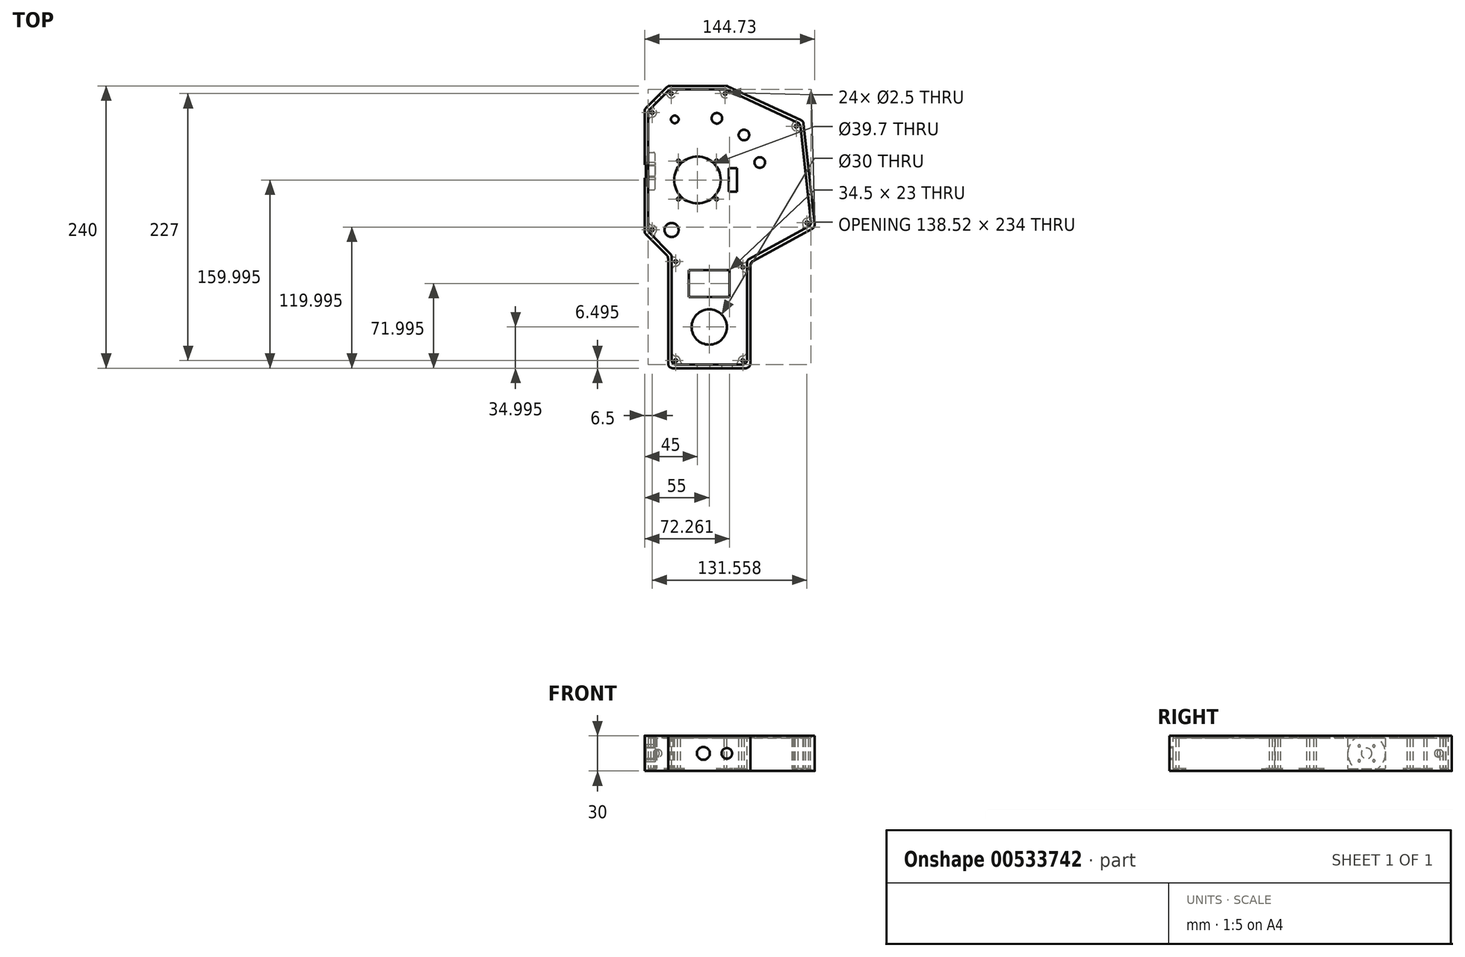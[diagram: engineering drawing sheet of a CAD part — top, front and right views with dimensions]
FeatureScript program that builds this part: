
annotation { "Feature Type Name" : "Feature", "Feature Type Description" : "" }
export const myFeature = defineFeature(function(context is Context, id is Id, definition is map)
    precondition{}
    {
        {
            var Q0;
            Q0=qCreatedBy(makeId("Top.planeOp"),FACE);
            var sketch = newSketch(context, id + "F0", { "sketchPlane" : qUnion([Q0])});
            skLineSegment(sketch, "E0", {"start": v(-66.45, 92.82) * mm, "end": v(-16.45, 92.82) * mm});
            skLineSegment(sketch, "E1", {"start": v(-16.45, 92.82) * mm, "end": v(48.55, 62.82) * mm});
            skLineSegment(sketch, "E2", {"start": v(48.55, 62.82) * mm, "end": v(58.55, -27.18) * mm});
            skLineSegment(sketch, "E3", {"start": v(58.55, -27.18) * mm, "end": v(3.55, -57.18) * mm});
            skLineSegment(sketch, "E4", {"start": v(3.55, -57.18) * mm, "end": v(3.55, -147.18) * mm});
            skLineSegment(sketch, "E5", {"start": v(3.55, -147.18) * mm, "end": v(-66.45, -147.18) * mm});
            skLineSegment(sketch, "E6", {"start": v(-66.45, -147.18) * mm, "end": v(-66.45, -52.18) * mm});
            skLineSegment(sketch, "E7", {"start": v(-66.45, -52.18) * mm, "end": v(-86.45, -32.18) * mm});
            skLineSegment(sketch, "E8", {"start": v(-86.45, -32.18) * mm, "end": v(-86.45, 72.82) * mm});
            skLineSegment(sketch, "E9", {"start": v(-86.45, 72.82) * mm, "end": v(-66.45, 92.82) * mm});
            skLineSegment(sketch, "E10.0", {"start": v(55.35, -25.52) * mm, "end": v(0.55, -55.4) * mm});
            skLineSegment(sketch, "E10.1", {"start": v(45.76, 60.8) * mm, "end": v(55.35, -25.52) * mm});
            skLineSegment(sketch, "E10.2", {"start": v(0.55, -55.4) * mm, "end": v(0.55, -144.18) * mm});
            skLineSegment(sketch, "E10.3", {"start": v(-17.1, 89.82) * mm, "end": v(45.76, 60.8) * mm});
            skLineSegment(sketch, "E10.4", {"start": v(-65.2, 89.82) * mm, "end": v(-17.1, 89.82) * mm});
            skLineSegment(sketch, "E10.5", {"start": v(-83.45, 71.57) * mm, "end": v(-65.2, 89.82) * mm});
            skLineSegment(sketch, "E10.6", {"start": v(0.55, -144.18) * mm, "end": v(-63.45, -144.18) * mm});
            skLineSegment(sketch, "E10.7", {"start": v(-63.45, -144.18) * mm, "end": v(-63.45, -50.94) * mm});
            skLineSegment(sketch, "E10.8", {"start": v(-63.45, -50.94) * mm, "end": v(-83.45, -30.94) * mm});
            skLineSegment(sketch, "E10.9", {"start": v(-83.45, -30.94) * mm, "end": v(-83.45, 71.57) * mm});
            skSolve(sketch);
        }
        {
            var Q0;
            Q0=makeQuery(id+"F0.imprint","IMPRINT",FACE,{"disambiguationData":[TD([[makeQuery(id+"F0.imprint","IMPRINT",EDGE,{"derivedFrom":sQuery(id+"F0.wireOp",EDGE,"E0")}),-1.0]])]});
            extrude(context, id + "F1", {"entities" : qUnion([Q0]), "endBound" : BoundingType.SYMMETRIC, "depth" : 30 * mm, "offsetDistance" : 25 * mm});
        }
        {
            var Q0;
            Q0=makeQuery(id+"F1.opExtrude","SWEPT_EDGE",EDGE,{"disambiguationData":[OSD([sQuery(id+"F0.wireOp",EDGE,"E4"),sQuery(id+"F0.wireOp",EDGE,"E5")])]});
            var Q1;
            Q1=makeQuery(id+"F1.opExtrude","SWEPT_EDGE",EDGE,{"disambiguationData":[OSD([sQuery(id+"F0.wireOp",EDGE,"E5"),sQuery(id+"F0.wireOp",EDGE,"E6")])]});
            var Q2;
            Q2=makeQuery(id+"F1.opExtrude","SWEPT_EDGE",EDGE,{"disambiguationData":[OSD([sQuery(id+"F0.wireOp",EDGE,"E6"),sQuery(id+"F0.wireOp",EDGE,"E7")])]});
            var Q3;
            Q3=makeQuery(id+"F1.opExtrude","SWEPT_EDGE",EDGE,{"disambiguationData":[OSD([sQuery(id+"F0.wireOp",EDGE,"E7"),sQuery(id+"F0.wireOp",EDGE,"E8")])]});
            var Q4;
            Q4=makeQuery(id+"F1.opExtrude","SWEPT_EDGE",EDGE,{"disambiguationData":[OSD([sQuery(id+"F0.wireOp",EDGE,"E8"),sQuery(id+"F0.wireOp",EDGE,"E9")])]});
            var Q5;
            Q5=makeQuery(id+"F1.opExtrude","SWEPT_EDGE",EDGE,{"disambiguationData":[OSD([sQuery(id+"F0.wireOp",EDGE,"E0"),sQuery(id+"F0.wireOp",EDGE,"E9")])]});
            var Q6;
            Q6=makeQuery(id+"F1.opExtrude","SWEPT_EDGE",EDGE,{"disambiguationData":[OSD([sQuery(id+"F0.wireOp",EDGE,"E0"),sQuery(id+"F0.wireOp",EDGE,"E1")])]});
            var Q7;
            Q7=makeQuery(id+"F1.opExtrude","SWEPT_EDGE",EDGE,{"disambiguationData":[OSD([sQuery(id+"F0.wireOp",EDGE,"E1"),sQuery(id+"F0.wireOp",EDGE,"E2")])]});
            var Q8;
            Q8=makeQuery(id+"F1.opExtrude","SWEPT_EDGE",EDGE,{"disambiguationData":[OSD([sQuery(id+"F0.wireOp",EDGE,"E2"),sQuery(id+"F0.wireOp",EDGE,"E3")])]});
            var Q9;
            Q9=makeQuery(id+"F1.opExtrude","SWEPT_EDGE",EDGE,{"disambiguationData":[OSD([sQuery(id+"F0.wireOp",EDGE,"E3"),sQuery(id+"F0.wireOp",EDGE,"E4")])]});
            var Q10;
            Q10=makeQuery(id+"F1.opExtrude","SWEPT_EDGE",EDGE,{"disambiguationData":[OSD([sQuery(id+"F0.wireOp",EDGE,"E10.5"),sQuery(id+"F0.wireOp",EDGE,"E10.9")])]});
            var Q11;
            Q11=makeQuery(id+"F1.opExtrude","SWEPT_EDGE",EDGE,{"disambiguationData":[OSD([sQuery(id+"F0.wireOp",EDGE,"E10.4"),sQuery(id+"F0.wireOp",EDGE,"E10.5")])]});
            var Q12;
            Q12=makeQuery(id+"F1.opExtrude","SWEPT_EDGE",EDGE,{"disambiguationData":[OSD([sQuery(id+"F0.wireOp",EDGE,"E10.3"),sQuery(id+"F0.wireOp",EDGE,"E10.4")])]});
            var Q13;
            Q13=makeQuery(id+"F1.opExtrude","SWEPT_EDGE",EDGE,{"disambiguationData":[OSD([sQuery(id+"F0.wireOp",EDGE,"E10.1"),sQuery(id+"F0.wireOp",EDGE,"E10.3")])]});
            var Q14;
            Q14=makeQuery(id+"F1.opExtrude","SWEPT_EDGE",EDGE,{"disambiguationData":[OSD([sQuery(id+"F0.wireOp",EDGE,"E10.0"),sQuery(id+"F0.wireOp",EDGE,"E10.1")])]});
            var Q15;
            Q15=makeQuery(id+"F1.opExtrude","SWEPT_EDGE",EDGE,{"disambiguationData":[OSD([sQuery(id+"F0.wireOp",EDGE,"E10.0"),sQuery(id+"F0.wireOp",EDGE,"E10.2")])]});
            var Q16;
            Q16=makeQuery(id+"F1.opExtrude","SWEPT_EDGE",EDGE,{"disambiguationData":[OSD([sQuery(id+"F0.wireOp",EDGE,"E10.7"),sQuery(id+"F0.wireOp",EDGE,"E10.8")])]});
            var Q17;
            Q17=makeQuery(id+"F1.opExtrude","SWEPT_EDGE",EDGE,{"disambiguationData":[OSD([sQuery(id+"F0.wireOp",EDGE,"E10.8"),sQuery(id+"F0.wireOp",EDGE,"E10.9")])]});
            var Q18;
            Q18=makeQuery(id+"F1.opExtrude","SWEPT_EDGE",EDGE,{"disambiguationData":[OSD([sQuery(id+"F0.wireOp",EDGE,"E10.6"),sQuery(id+"F0.wireOp",EDGE,"E10.7")])]});
            var Q19;
            Q19=makeQuery(id+"F1.opExtrude","SWEPT_EDGE",EDGE,{"disambiguationData":[OSD([sQuery(id+"F0.wireOp",EDGE,"E10.2"),sQuery(id+"F0.wireOp",EDGE,"E10.6")])]});
            fillet(context, id + "F2", {"entities" : qUnion([Q0, Q1, Q2, Q3, Q4, Q5, Q6, Q7, Q8, Q9, Q10, Q11, Q12, Q13, Q14, Q15, Q16, Q17, Q18, Q19]), "radius" : 4 * mm, "tangentPropagation" : true, "allowEdgeOverflow" : false});
        }
        {
            var Q0;
            Q0=qCreatedBy(makeId("Top.planeOp"),FACE);
            var sketch = newSketch(context, id + "F3", { "sketchPlane" : qUnion([Q0])});
            skLineSegment(sketch, "E11.0", {"start": v(-84.95, -31.56) * mm, "end": v(-84.95, 72.2) * mm, "construction": true});
            skLineSegment(sketch, "E11.1", {"start": v(-64.95, -51.56) * mm, "end": v(-84.95, -31.56) * mm, "construction": true});
            skLineSegment(sketch, "E11.2", {"start": v(-84.95, 72.2) * mm, "end": v(-65.83, 91.32) * mm, "construction": true});
            skLineSegment(sketch, "E11.3", {"start": v(-64.95, -145.68) * mm, "end": v(-64.95, -51.56) * mm, "construction": true});
            skLineSegment(sketch, "E11.4", {"start": v(2.05, -145.68) * mm, "end": v(-64.95, -145.68) * mm, "construction": true});
            skLineSegment(sketch, "E11.5", {"start": v(2.05, -56.3) * mm, "end": v(2.05, -145.68) * mm, "construction": true});
            skLineSegment(sketch, "E11.6", {"start": v(-65.83, 91.32) * mm, "end": v(-16.78, 91.32) * mm, "construction": true});
            skLineSegment(sketch, "E11.7", {"start": v(-16.78, 91.32) * mm, "end": v(47.15, 61.8) * mm, "construction": true});
            skLineSegment(sketch, "E11.8", {"start": v(47.15, 61.8) * mm, "end": v(56.95, -26.35) * mm, "construction": true});
            skLineSegment(sketch, "E11.9", {"start": v(56.95, -26.35) * mm, "end": v(2.05, -56.3) * mm, "construction": true});
            skSolve(sketch);
        }
        {
            var Q0;
            Q0=qCreatedBy(makeId("Top.planeOp"),FACE);
            var sketch = newSketch(context, id + "F4", { "sketchPlane" : qUnion([Q0])});
            skCircle(sketch, "E12", {"center": v(-79.95, 70.12) * mm, "radius": 3.75 * mm});
            skCircle(sketch, "E13", {"center": v(-79.95, 70.12) * mm, "radius": 1.25 * mm});
            skCircle(sketch, "E14", {"center": v(-63.76, 86.32) * mm, "radius": 3.75 * mm});
            skCircle(sketch, "E15", {"center": v(-63.76, 86.32) * mm, "radius": 1.25 * mm});
            skCircle(sketch, "E16", {"center": v(-17.88, 86.32) * mm, "radius": 3.75 * mm});
            skCircle(sketch, "E17", {"center": v(-17.88, 86.32) * mm, "radius": 1.25 * mm});
            skCircle(sketch, "E18", {"center": v(42.5, 58.45) * mm, "radius": 3.75 * mm});
            skCircle(sketch, "E19", {"center": v(42.5, 58.45) * mm, "radius": 1.25 * mm});
            skCircle(sketch, "E20", {"center": v(51.6, -23.57) * mm, "radius": 3.75 * mm});
            skCircle(sketch, "E21", {"center": v(51.6, -23.57) * mm, "radius": 1.25 * mm});
            skCircle(sketch, "E22", {"center": v(-2.95, -140.68) * mm, "radius": 3.75 * mm});
            skCircle(sketch, "E23", {"center": v(-2.95, -140.68) * mm, "radius": 1.25 * mm});
            skCircle(sketch, "E24", {"center": v(-59.95, -140.68) * mm, "radius": 3.75 * mm});
            skCircle(sketch, "E25", {"center": v(-59.95, -140.68) * mm, "radius": 1.25 * mm});
            skCircle(sketch, "E26", {"center": v(-79.95, -29.5) * mm, "radius": 3.75 * mm});
            skCircle(sketch, "E27", {"center": v(-79.95, -29.5) * mm, "radius": 1.25 * mm});
            skCircle(sketch, "E28", {"center": v(-59.95, -56.56) * mm, "radius": 3.75 * mm});
            skCircle(sketch, "E29", {"center": v(-59.95, -56.56) * mm, "radius": 1.25 * mm});
            skCircle(sketch, "E30", {"center": v(-2.95, -61.3) * mm, "radius": 3.75 * mm});
            skCircle(sketch, "E31", {"center": v(-2.95, -61.3) * mm, "radius": 1.25 * mm});
            skLineSegment(sketch, "E32.bottom", {"start": v(-83.45, 4.32) * mm, "end": v(-77.45, 4.32) * mm});
            skLineSegment(sketch, "E32.top", {"start": v(-83.45, 36.32) * mm, "end": v(-77.45, 36.32) * mm});
            skLineSegment(sketch, "E32.left", {"start": v(-83.45, 4.32) * mm, "end": v(-83.45, 36.32) * mm});
            skLineSegment(sketch, "E32.right", {"start": v(-77.45, 4.32) * mm, "end": v(-77.45, 36.32) * mm});
            skSolve(sketch);
        }
        {
            var Q0;
            Q0=makeQuery(id+"F4.imprint","IMPRINT",FACE,{"disambiguationData":[TD([[makeQuery(id+"F4.imprint","IMPRINT",EDGE,{"derivedFrom":sQuery(id+"F4.wireOp",EDGE,"E24")}),1.0]])]});
            var Q1;
            Q1=makeQuery(id+"F4.imprint","IMPRINT",FACE,{"disambiguationData":[TD([[makeQuery(id+"F4.imprint","IMPRINT",EDGE,{"derivedFrom":sQuery(id+"F4.wireOp",EDGE,"E22")}),1.0]])]});
            var Q2;
            Q2=makeQuery(id+"F4.imprint","IMPRINT",FACE,{"disambiguationData":[TD([[makeQuery(id+"F4.imprint","IMPRINT",EDGE,{"derivedFrom":sQuery(id+"F4.wireOp",EDGE,"E30")}),1.0]])]});
            var Q3;
            Q3=makeQuery(id+"F4.imprint","IMPRINT",FACE,{"disambiguationData":[TD([[makeQuery(id+"F4.imprint","IMPRINT",EDGE,{"derivedFrom":sQuery(id+"F4.wireOp",EDGE,"E28")}),1.0]])]});
            var Q4;
            Q4=makeQuery(id+"F4.imprint","IMPRINT",FACE,{"disambiguationData":[TD([[makeQuery(id+"F4.imprint","IMPRINT",EDGE,{"derivedFrom":sQuery(id+"F4.wireOp",EDGE,"E26")}),1.0]])]});
            var Q5;
            Q5=makeQuery(id+"F4.imprint","IMPRINT",FACE,{"disambiguationData":[TD([[makeQuery(id+"F4.imprint","IMPRINT",EDGE,{"derivedFrom":sQuery(id+"F4.wireOp",EDGE,"E20")}),1.0]])]});
            var Q6;
            Q6=makeQuery(id+"F4.imprint","IMPRINT",FACE,{"disambiguationData":[TD([[makeQuery(id+"F4.imprint","IMPRINT",EDGE,{"derivedFrom":sQuery(id+"F4.wireOp",EDGE,"E18")}),1.0]])]});
            var Q7;
            Q7=makeQuery(id+"F4.imprint","IMPRINT",FACE,{"disambiguationData":[TD([[makeQuery(id+"F4.imprint","IMPRINT",EDGE,{"derivedFrom":sQuery(id+"F4.wireOp",EDGE,"E16")}),1.0]])]});
            var Q8;
            Q8=makeQuery(id+"F4.imprint","IMPRINT",FACE,{"disambiguationData":[TD([[makeQuery(id+"F4.imprint","IMPRINT",EDGE,{"derivedFrom":sQuery(id+"F4.wireOp",EDGE,"E14")}),1.0]])]});
            var Q9;
            Q9=makeQuery(id+"F4.imprint","IMPRINT",FACE,{"disambiguationData":[TD([[makeQuery(id+"F4.imprint","IMPRINT",EDGE,{"derivedFrom":sQuery(id+"F4.wireOp",EDGE,"E12")}),1.0]])]});
            var Q10;
            Q10=makeQuery(id+"F4.imprint","IMPRINT",FACE,{"disambiguationData":[TD([[makeQuery(id+"F4.imprint","IMPRINT",EDGE,{"derivedFrom":sQuery(id+"F4.wireOp",EDGE,"E32.bottom")}),1.0]])]});
            extrude(context, id + "F5", {"entities" : qUnion([Q0, Q1, Q2, Q3, Q4, Q5, Q6, Q7, Q8, Q9, Q10]), "operationType" : NewBodyOperationType.ADD, "endBound" : BoundingType.SYMMETRIC, "depth" : 26 * mm, "offsetDistance" : 25 * mm});
        }
        {
            var Q0;
            Q0=makeQuery(id+"F5.boolean.opBoolean","INTERSECT",EDGE,{"disambiguationData":[OD(0.0)],"derivedFrom":[makeQuery(id+"F1.opExtrude","SWEPT_FACE",FACE,{"disambiguationData":[OSD([sQuery(id+"F0.wireOp",EDGE,"E10.7")])]}),makeQuery(id+"F5.opExtrude","SWEPT_FACE",FACE,{"disambiguationData":[OSD([sQuery(id+"F4.wireOp",EDGE,"E28")])]})]});
            var Q1;
            Q1=makeQuery(id+"F5.boolean.opBoolean","INTERSECT",EDGE,{"disambiguationData":[OD(1.0)],"derivedFrom":[makeQuery(id+"F1.opExtrude","SWEPT_FACE",FACE,{"disambiguationData":[OSD([sQuery(id+"F0.wireOp",EDGE,"E10.7")])]}),makeQuery(id+"F5.opExtrude","SWEPT_FACE",FACE,{"disambiguationData":[OSD([sQuery(id+"F4.wireOp",EDGE,"E28")])]})]});
            var Q2;
            Q2=makeQuery(id+"F5.boolean.opBoolean","INTERSECT",EDGE,{"derivedFrom":[makeQuery(id+"F1.opExtrude","SWEPT_FACE",FACE,{"disambiguationData":[OSD([sQuery(id+"F0.wireOp",EDGE,"E10.9")])]}),makeQuery(id+"F5.opExtrude","SWEPT_FACE",FACE,{"disambiguationData":[OSD([sQuery(id+"F4.wireOp",EDGE,"E12")])]})]});
            var Q3;
            Q3=makeQuery(id+"F5.boolean.opBoolean","INTERSECT",EDGE,{"derivedFrom":[makeQuery(id+"F1.opExtrude","SWEPT_FACE",FACE,{"disambiguationData":[OSD([sQuery(id+"F0.wireOp",EDGE,"E10.4")])]}),makeQuery(id+"F5.opExtrude","SWEPT_FACE",FACE,{"disambiguationData":[OSD([sQuery(id+"F4.wireOp",EDGE,"E16")])]})]});
            var Q4;
            Q4=makeQuery(id+"F5.boolean.opBoolean","INTERSECT",EDGE,{"derivedFrom":[makeQuery(id+"F1.opExtrude","SWEPT_FACE",FACE,{"disambiguationData":[OSD([sQuery(id+"F0.wireOp",EDGE,"E10.4")])]}),makeQuery(id+"F5.opExtrude","SWEPT_FACE",FACE,{"disambiguationData":[OSD([sQuery(id+"F4.wireOp",EDGE,"E14")])]})]});
            var Q5;
            Q5=makeQuery(id+"F5.boolean.opBoolean","INTERSECT",EDGE,{"derivedFrom":[makeQuery(id+"F1.opExtrude","SWEPT_FACE",FACE,{"disambiguationData":[OSD([sQuery(id+"F0.wireOp",EDGE,"E10.1")])]}),makeQuery(id+"F5.opExtrude","SWEPT_FACE",FACE,{"disambiguationData":[OSD([sQuery(id+"F4.wireOp",EDGE,"E18")])]})]});
            var Q6;
            Q6=makeQuery(id+"F5.boolean.opBoolean","INTERSECT",EDGE,{"derivedFrom":[makeQuery(id+"F1.opExtrude","SWEPT_FACE",FACE,{"disambiguationData":[OSD([sQuery(id+"F0.wireOp",EDGE,"E10.0")])]}),makeQuery(id+"F5.opExtrude","SWEPT_FACE",FACE,{"disambiguationData":[OSD([sQuery(id+"F4.wireOp",EDGE,"E20")])]})]});
            var Q7;
            Q7=makeQuery(id+"F5.boolean.opBoolean","INTERSECT",EDGE,{"derivedFrom":[makeQuery(id+"F1.opExtrude","SWEPT_FACE",FACE,{"disambiguationData":[OSD([sQuery(id+"F0.wireOp",EDGE,"E10.1")])]}),makeQuery(id+"F5.opExtrude","SWEPT_FACE",FACE,{"disambiguationData":[OSD([sQuery(id+"F4.wireOp",EDGE,"E20")])]})]});
            var Q8;
            Q8=makeQuery(id+"F5.boolean.opBoolean","INTERSECT",EDGE,{"derivedFrom":[makeQuery(id+"F1.opExtrude","SWEPT_FACE",FACE,{"disambiguationData":[OSD([sQuery(id+"F0.wireOp",EDGE,"E10.8")])]}),makeQuery(id+"F5.opExtrude","SWEPT_FACE",FACE,{"disambiguationData":[OSD([sQuery(id+"F4.wireOp",EDGE,"E26")])]})]});
            var Q9;
            Q9=makeQuery(id+"F5.boolean.opBoolean","INTERSECT",EDGE,{"derivedFrom":[makeQuery(id+"F1.opExtrude","SWEPT_FACE",FACE,{"disambiguationData":[OSD([sQuery(id+"F0.wireOp",EDGE,"E10.9")])]}),makeQuery(id+"F5.opExtrude","SWEPT_FACE",FACE,{"disambiguationData":[OSD([sQuery(id+"F4.wireOp",EDGE,"E26")])]})]});
            var Q10;
            Q10=makeQuery(id+"F5.boolean.opBoolean","INTERSECT",EDGE,{"derivedFrom":[makeQuery(id+"F1.opExtrude","SWEPT_FACE",FACE,{"disambiguationData":[OSD([sQuery(id+"F0.wireOp",EDGE,"E10.7")])]}),makeQuery(id+"F5.opExtrude","SWEPT_FACE",FACE,{"disambiguationData":[OSD([sQuery(id+"F4.wireOp",EDGE,"E24")])]})]});
            var Q11;
            Q11=makeQuery(id+"F5.boolean.opBoolean","INTERSECT",EDGE,{"derivedFrom":[makeQuery(id+"F1.opExtrude","SWEPT_FACE",FACE,{"disambiguationData":[OSD([sQuery(id+"F0.wireOp",EDGE,"E10.6")])]}),makeQuery(id+"F5.opExtrude","SWEPT_FACE",FACE,{"disambiguationData":[OSD([sQuery(id+"F4.wireOp",EDGE,"E24")])]})]});
            var Q12;
            Q12=makeQuery(id+"F5.boolean.opBoolean","INTERSECT",EDGE,{"derivedFrom":[makeQuery(id+"F1.opExtrude","SWEPT_FACE",FACE,{"disambiguationData":[OSD([sQuery(id+"F0.wireOp",EDGE,"E10.6")])]}),makeQuery(id+"F5.opExtrude","SWEPT_FACE",FACE,{"disambiguationData":[OSD([sQuery(id+"F4.wireOp",EDGE,"E22")])]})]});
            var Q13;
            Q13=makeQuery(id+"F5.boolean.opBoolean","INTERSECT",EDGE,{"derivedFrom":[makeQuery(id+"F1.opExtrude","SWEPT_FACE",FACE,{"disambiguationData":[OSD([sQuery(id+"F0.wireOp",EDGE,"E10.2")])]}),makeQuery(id+"F5.opExtrude","SWEPT_FACE",FACE,{"disambiguationData":[OSD([sQuery(id+"F4.wireOp",EDGE,"E22")])]})]});
            var Q14;
            Q14=makeQuery(id+"F5.boolean.opBoolean","INTERSECT",EDGE,{"disambiguationData":[OD(0.0)],"derivedFrom":[makeQuery(id+"F1.opExtrude","SWEPT_FACE",FACE,{"disambiguationData":[OSD([sQuery(id+"F0.wireOp",EDGE,"E10.2")])]}),makeQuery(id+"F5.opExtrude","SWEPT_FACE",FACE,{"disambiguationData":[OSD([sQuery(id+"F4.wireOp",EDGE,"E30")])]})]});
            var Q15;
            Q15=makeQuery(id+"F5.boolean.opBoolean","INTERSECT",EDGE,{"disambiguationData":[OD(1.0)],"derivedFrom":[makeQuery(id+"F1.opExtrude","SWEPT_FACE",FACE,{"disambiguationData":[OSD([sQuery(id+"F0.wireOp",EDGE,"E10.2")])]}),makeQuery(id+"F5.opExtrude","SWEPT_FACE",FACE,{"disambiguationData":[OSD([sQuery(id+"F4.wireOp",EDGE,"E30")])]})]});
            var Q16;
            Q16=makeQuery(id+"F5.opExtrude","SWEPT_EDGE",EDGE,{"disambiguationData":[OSD([sQuery(id+"F4.wireOp",EDGE,"E32.bottom"),sQuery(id+"F4.wireOp",EDGE,"E32.left")])]});
            var Q17;
            Q17=makeQuery(id+"F5.opExtrude","SWEPT_EDGE",EDGE,{"disambiguationData":[OSD([sQuery(id+"F4.wireOp",EDGE,"E32.top"),sQuery(id+"F4.wireOp",EDGE,"E32.left")])]});
            fillet(context, id + "F6", {"entities" : qUnion([Q0, Q1, Q2, Q3, Q4, Q5, Q6, Q7, Q8, Q9, Q10, Q11, Q12, Q13, Q14, Q15, Q16, Q17]), "radius" : 4 * mm, "tangentPropagation" : true, "allowEdgeOverflow" : false});
        }
        {
            var Q0;
            Q0=makeQuery(id+"F1.opExtrude","SWEPT_FACE",FACE,{"disambiguationData":[OSD([sQuery(id+"F0.wireOp",EDGE,"E5")])]});
            var sketch = newSketch(context, id + "F7", { "sketchPlane" : qUnion([Q0])});
            skCircle(sketch, "E33", {"center": v(-16.45, 0) * mm, "radius": 4.5 * mm});
            skCircle(sketch, "E34", {"center": v(-36.45, 0) * mm, "radius": 5.5 * mm});
            skSolve(sketch);
        }
        {
            var Q0;
            Q0=makeQuery(id+"F7.imprint","IMPRINT",FACE,{"disambiguationData":[TD([[makeQuery(id+"F7.imprint","IMPRINT",EDGE,{"derivedFrom":sQuery(id+"F7.wireOp",EDGE,"E34")}),1.0]])]});
            var Q1;
            Q1=makeQuery(id+"F7.imprint","IMPRINT",FACE,{"disambiguationData":[TD([[makeQuery(id+"F7.imprint","IMPRINT",EDGE,{"derivedFrom":sQuery(id+"F7.wireOp",EDGE,"E33")}),1.0]])]});
            extrude(context, id + "F8", {"entities" : qUnion([Q0, Q1]), "operationType" : NewBodyOperationType.REMOVE, "oppositeDirection" : true, "depth" : 3 * mm, "offsetDistance" : 25 * mm});
        }
        {
            var Q0;
            Q0=makeQuery(id+"F1.opExtrude","SWEPT_FACE",FACE,{"disambiguationData":[OSD([sQuery(id+"F0.wireOp",EDGE,"E8")])]});
            var sketch = newSketch(context, id + "F9", { "sketchPlane" : qUnion([Q0])});
            skCircle(sketch, "E35", {"center": v(-20.32, 0) * mm, "radius": 16 * mm});
            skSolve(sketch);
        }
        {
            var Q0;
            {var subQ0=sQuery(id+"F9.wireOp",EDGE,"E35");var subQ1=sQuery(id+"F0.wireOp",EDGE,"E8");var subQ2=makeQuery(id+"F1.opExtrude","CAP_EDGE",EDGE,{"disambiguationData":[OSD([subQ1])],"isStart":false});var subQ3=makeQuery(id+"F9.imprint","INTERSECT",VERTEX,{"disambiguationData":[OD(0.0)],"derivedFrom":[subQ2,subQ0]});Q0=makeQuery(id+"F9.imprint","IMPRINT",FACE,{"disambiguationData":[TD([[makeQuery(id+"F9.imprint","IMPRINT",EDGE,{"disambiguationData":[TD([[subQ3,-1.0]])],"derivedFrom":subQ0}),1.0]])]});}
            extrude(context, id + "F10", {"entities" : qUnion([Q0]), "operationType" : NewBodyOperationType.REMOVE, "oppositeDirection" : true, "depth" : 1 * mm, "offsetDistance" : 25 * mm});
        }
        {
            var Q0;
            Q0=makeQuery(id+"F10.boolean.opBoolean","COPY",FACE,{"derivedFrom":makeQuery(id+"F10.opExtrude","CAP_FACE",FACE,{"disambiguationData":[OSD([sQuery(id+"F0.wireOp",EDGE,"E8"),sQuery(id+"F9.wireOp",EDGE,"E35")])],"isStart":false})});
            var sketch = newSketch(context, id + "F11", { "sketchPlane" : qUnion([Q0])});
            skCircle(sketch, "E36", {"center": v(-20.32, 0) * mm, "radius": 4.5 * mm});
            skCircle(sketch, "E37", {"center": v(-26.57, 6.25) * mm, "radius": 1 * mm});
            skCircle(sketch, "E38", {"center": v(-14.07, 6.25) * mm, "radius": 1 * mm});
            skCircle(sketch, "E39", {"center": v(-14.07, -6.25) * mm, "radius": 1 * mm});
            skCircle(sketch, "E40", {"center": v(-26.57, -6.25) * mm, "radius": 1 * mm});
            skSolve(sketch);
        }
        {
            var Q0;
            Q0=makeQuery(id+"F11.imprint","IMPRINT",FACE,{"disambiguationData":[TD([[makeQuery(id+"F11.imprint","IMPRINT",EDGE,{"derivedFrom":sQuery(id+"F11.wireOp",EDGE,"E37")}),1.0]])]});
            var Q1;
            Q1=makeQuery(id+"F11.imprint","IMPRINT",FACE,{"disambiguationData":[TD([[makeQuery(id+"F11.imprint","IMPRINT",EDGE,{"derivedFrom":sQuery(id+"F11.wireOp",EDGE,"E38")}),1.0]])]});
            var Q2;
            Q2=makeQuery(id+"F11.imprint","IMPRINT",FACE,{"disambiguationData":[TD([[makeQuery(id+"F11.imprint","IMPRINT",EDGE,{"derivedFrom":sQuery(id+"F11.wireOp",EDGE,"E36")}),1.0]])]});
            var Q3;
            Q3=makeQuery(id+"F11.imprint","IMPRINT",FACE,{"disambiguationData":[TD([[makeQuery(id+"F11.imprint","IMPRINT",EDGE,{"derivedFrom":sQuery(id+"F11.wireOp",EDGE,"E39")}),1.0]])]});
            var Q4;
            Q4=makeQuery(id+"F11.imprint","IMPRINT",FACE,{"disambiguationData":[TD([[makeQuery(id+"F11.imprint","IMPRINT",EDGE,{"derivedFrom":sQuery(id+"F11.wireOp",EDGE,"E40")}),1.0]])]});
            extrude(context, id + "F12", {"entities" : qUnion([Q0, Q1, Q2, Q3, Q4]), "operationType" : NewBodyOperationType.REMOVE, "depth" : -8.5 * mm, "offsetDistance" : 25 * mm});
        }
        {
            var Q0;
            Q0=makeQuery(id+"F5.opExtrude","SWEPT_EDGE",EDGE,{"disambiguationData":[OSD([sQuery(id+"F4.wireOp",EDGE,"E32.bottom"),sQuery(id+"F4.wireOp",EDGE,"E32.right")])]});
            var Q1;
            Q1=makeQuery(id+"F5.opExtrude","SWEPT_EDGE",EDGE,{"disambiguationData":[OSD([sQuery(id+"F4.wireOp",EDGE,"E32.top"),sQuery(id+"F4.wireOp",EDGE,"E32.right")])]});
            fillet(context, id + "F13", {"entities" : qUnion([Q0, Q1]), "radius" : 1.5 * mm, "tangentPropagation" : true, "allowEdgeOverflow" : false});
        }
        {
            var Q0;
            Q0=makeQuery(id+"F1.opExtrude","SWEPT_FACE",FACE,{"disambiguationData":[OSD([sQuery(id+"F0.wireOp",EDGE,"E9")])]});
            var sketch = newSketch(context, id + "F14", { "sketchPlane" : qUnion([Q0])});
            skCircle(sketch, "E41", {"center": v(-4.5, 0) * mm, "radius": 3.25 * mm});
            skPoint(sketch, "E41.centerSnap0", {"position": v(-4.5, 15) * mm});
            skSolve(sketch);
        }
        {
            var Q0;
            Q0=makeQuery(id+"F14.imprint","IMPRINT",FACE,{"disambiguationData":[TD([[makeQuery(id+"F14.imprint","IMPRINT",EDGE,{"derivedFrom":sQuery(id+"F14.wireOp",EDGE,"E41")}),1.0]])]});
            extrude(context, id + "F15", {"entities" : qUnion([Q0]), "operationType" : NewBodyOperationType.REMOVE, "oppositeDirection" : true, "depth" : 3 * mm, "offsetDistance" : 25 * mm});
        }
        {
            var Q0;
            Q0=makeQuery(id+"F5.boolean.opBoolean","INTERSECT",EDGE,{"derivedFrom":[makeQuery(id+"F1.opExtrude","SWEPT_FACE",FACE,{"disambiguationData":[OSD([sQuery(id+"F0.wireOp",EDGE,"E10.5")])]}),makeQuery(id+"F5.opExtrude","SWEPT_FACE",FACE,{"disambiguationData":[OSD([sQuery(id+"F4.wireOp",EDGE,"E14")])]})]});
            var Q1;
            Q1=makeQuery(id+"F5.boolean.opBoolean","INTERSECT",EDGE,{"derivedFrom":[makeQuery(id+"F1.opExtrude","SWEPT_FACE",FACE,{"disambiguationData":[OSD([sQuery(id+"F0.wireOp",EDGE,"E10.5")])]}),makeQuery(id+"F5.opExtrude","SWEPT_FACE",FACE,{"disambiguationData":[OSD([sQuery(id+"F4.wireOp",EDGE,"E12")])]})]});
            var Q2;
            Q2=makeQuery(id+"F5.boolean.opBoolean","INTERSECT",EDGE,{"derivedFrom":[makeQuery(id+"F1.opExtrude","SWEPT_FACE",FACE,{"disambiguationData":[OSD([sQuery(id+"F0.wireOp",EDGE,"E10.3")])]}),makeQuery(id+"F5.opExtrude","SWEPT_FACE",FACE,{"disambiguationData":[OSD([sQuery(id+"F4.wireOp",EDGE,"E18")])]})]});
            var Q3;
            Q3=makeQuery(id+"F5.boolean.opBoolean","INTERSECT",EDGE,{"derivedFrom":[makeQuery(id+"F1.opExtrude","SWEPT_FACE",FACE,{"disambiguationData":[OSD([sQuery(id+"F0.wireOp",EDGE,"E10.3")])]}),makeQuery(id+"F5.opExtrude","SWEPT_FACE",FACE,{"disambiguationData":[OSD([sQuery(id+"F4.wireOp",EDGE,"E16")])]})]});
            fillet(context, id + "F16", {"entities" : qUnion([Q0, Q1, Q2, Q3]), "radius" : 2 * mm, "tangentPropagation" : true, "allowEdgeOverflow" : false});
        }
        {
            var Q0;
            Q0=makeQuery(id+"F5.opExtrude","CAP_FACE",FACE,{"disambiguationData":[OSD([sQuery(id+"F4.wireOp",EDGE,"E14"),sQuery(id+"F4.wireOp",EDGE,"E15")])],"isStart":false});
            var sketch = newSketch(context, id + "F17", { "sketchPlane" : qUnion([Q0])});
            skLineSegment(sketch, "E42.0", {"start": v(-63.55, 89.82) * mm, "end": v(-17.99, 89.82) * mm});
            skArc(sketch, "E42.1", {"start": v(-17.99, 89.82) * mm, "mid": v(-17.13, 89.72) * mm, "end": v(-16.31, 89.45) * mm});
            skLineSegment(sketch, "E42.2", {"start": v(-16.31, 89.45) * mm, "end": v(43.7, 61.75) * mm});
            skArc(sketch, "E42.3", {"start": v(-66.38, 88.64) * mm, "mid": v(-65.08, 89.51) * mm, "end": v(-63.55, 89.82) * mm});
            skLineSegment(sketch, "E42.4", {"start": v(-82.28, 72.74) * mm, "end": v(-66.38, 88.64) * mm});
            skArc(sketch, "E42.5", {"start": v(-83.45, 69.92) * mm, "mid": v(-83.15, 71.45) * mm, "end": v(-82.28, 72.74) * mm});
            skLineSegment(sketch, "E42.6", {"start": v(-83.45, -29.29) * mm, "end": v(-83.45, 69.92) * mm});
            skArc(sketch, "E42.7", {"start": v(-82.28, -32.11) * mm, "mid": v(-83.15, -30.82) * mm, "end": v(-83.45, -29.29) * mm});
            skLineSegment(sketch, "E42.8", {"start": v(-64.62, -49.77) * mm, "end": v(-82.28, -32.11) * mm});
            skArc(sketch, "E42.9", {"start": v(-63.45, -52.6) * mm, "mid": v(-63.75, -51.07) * mm, "end": v(-64.62, -49.77) * mm});
            skLineSegment(sketch, "E42.10", {"start": v(-63.45, -140.18) * mm, "end": v(-63.45, -52.6) * mm});
            skArc(sketch, "E42.11", {"start": v(-59.45, -144.18) * mm, "mid": v(-62.28, -143.01) * mm, "end": v(-63.45, -140.18) * mm});
            skLineSegment(sketch, "E42.12", {"start": v(-3.45, -144.18) * mm, "end": v(-59.45, -144.18) * mm});
            skArc(sketch, "E42.13", {"start": v(0.55, -140.18) * mm, "mid": v(-0.62, -143.01) * mm, "end": v(-3.45, -144.18) * mm});
            skLineSegment(sketch, "E42.14", {"start": v(0.55, -57.78) * mm, "end": v(0.55, -140.18) * mm});
            skArc(sketch, "E42.15", {"start": v(2.63, -54.27) * mm, "mid": v(1.11, -55.74) * mm, "end": v(0.55, -57.78) * mm});
            skLineSegment(sketch, "E42.16", {"start": v(52.99, -26.8) * mm, "end": v(2.63, -54.27) * mm});
            skArc(sketch, "E42.17", {"start": v(55.05, -22.85) * mm, "mid": v(54.62, -25.14) * mm, "end": v(52.99, -26.8) * mm});
            skLineSegment(sketch, "E42.18", {"start": v(46, 58.56) * mm, "end": v(55.05, -22.85) * mm});
            skArc(sketch, "E42.19", {"start": v(43.7, 61.75) * mm, "mid": v(45.27, 60.45) * mm, "end": v(46, 58.56) * mm});
            skSolve(sketch);
        }
        {
            var Q0;
            Q0 = qSketchRegion(id + "F17", true);
            extrude(context, id + "F18", {"entities" : qUnion([Q0]), "depth" : 2 * mm, "offsetDistance" : 25 * mm});
        }
        {
            var Q0;
            Q0=makeQuery(id+"F4.imprint","IMPRINT",FACE,{"disambiguationData":[TD([[makeQuery(id+"F4.imprint","IMPRINT",EDGE,{"derivedFrom":sQuery(id+"F4.wireOp",EDGE,"E13")}),1.0]])]});
            var Q1;
            Q1=makeQuery(id+"F4.imprint","IMPRINT",FACE,{"disambiguationData":[TD([[makeQuery(id+"F4.imprint","IMPRINT",EDGE,{"derivedFrom":sQuery(id+"F4.wireOp",EDGE,"E27")}),1.0]])]});
            var Q2;
            Q2=makeQuery(id+"F4.imprint","IMPRINT",FACE,{"disambiguationData":[TD([[makeQuery(id+"F4.imprint","IMPRINT",EDGE,{"derivedFrom":sQuery(id+"F4.wireOp",EDGE,"E29")}),1.0]])]});
            var Q3;
            Q3=makeQuery(id+"F4.imprint","IMPRINT",FACE,{"disambiguationData":[TD([[makeQuery(id+"F4.imprint","IMPRINT",EDGE,{"derivedFrom":sQuery(id+"F4.wireOp",EDGE,"E31")}),1.0]])]});
            var Q4;
            Q4=makeQuery(id+"F4.imprint","IMPRINT",FACE,{"disambiguationData":[TD([[makeQuery(id+"F4.imprint","IMPRINT",EDGE,{"derivedFrom":sQuery(id+"F4.wireOp",EDGE,"E21")}),1.0]])]});
            var Q5;
            Q5=makeQuery(id+"F4.imprint","IMPRINT",FACE,{"disambiguationData":[TD([[makeQuery(id+"F4.imprint","IMPRINT",EDGE,{"derivedFrom":sQuery(id+"F4.wireOp",EDGE,"E25")}),1.0]])]});
            var Q6;
            Q6=makeQuery(id+"F4.imprint","IMPRINT",FACE,{"disambiguationData":[TD([[makeQuery(id+"F4.imprint","IMPRINT",EDGE,{"derivedFrom":sQuery(id+"F4.wireOp",EDGE,"E23")}),1.0]])]});
            var Q7;
            Q7=makeQuery(id+"F4.imprint","IMPRINT",FACE,{"disambiguationData":[TD([[makeQuery(id+"F4.imprint","IMPRINT",EDGE,{"derivedFrom":sQuery(id+"F4.wireOp",EDGE,"E17")}),1.0]])]});
            var Q8;
            Q8=makeQuery(id+"F4.imprint","IMPRINT",FACE,{"disambiguationData":[TD([[makeQuery(id+"F4.imprint","IMPRINT",EDGE,{"derivedFrom":sQuery(id+"F4.wireOp",EDGE,"E15")}),1.0]])]});
            var Q9;
            Q9=makeQuery(id+"F4.imprint","IMPRINT",FACE,{"disambiguationData":[TD([[makeQuery(id+"F4.imprint","IMPRINT",EDGE,{"derivedFrom":sQuery(id+"F4.wireOp",EDGE,"E19")}),1.0]])]});
            extrude(context, id + "F19", {"entities" : qUnion([Q0, Q1, Q2, Q3, Q4, Q5, Q6, Q7, Q8, Q9]), "operationType" : NewBodyOperationType.REMOVE, "depth" : 25 * mm, "offsetDistance" : 25 * mm});
        }
        {
            var Q0;
            Q0=makeQuery(id+"F18.opExtrude","CAP_FACE",FACE,{"disambiguationData":[OSD([sQuery(id+"F17.wireOp",EDGE,"E42.0"),sQuery(id+"F17.wireOp",EDGE,"E42.1"),sQuery(id+"F17.wireOp",EDGE,"E42.2"),sQuery(id+"F17.wireOp",EDGE,"E42.3"),sQuery(id+"F17.wireOp",EDGE,"E42.4"),sQuery(id+"F17.wireOp",EDGE,"E42.5"),sQuery(id+"F17.wireOp",EDGE,"E42.6"),sQuery(id+"F17.wireOp",EDGE,"E42.7"),sQuery(id+"F17.wireOp",EDGE,"E42.8"),sQuery(id+"F17.wireOp",EDGE,"E42.9"),sQuery(id+"F17.wireOp",EDGE,"E42.10"),sQuery(id+"F17.wireOp",EDGE,"E42.11"),sQuery(id+"F17.wireOp",EDGE,"E42.12"),sQuery(id+"F17.wireOp",EDGE,"E42.13"),sQuery(id+"F17.wireOp",EDGE,"E42.14"),sQuery(id+"F17.wireOp",EDGE,"E42.15"),sQuery(id+"F17.wireOp",EDGE,"E42.16"),sQuery(id+"F17.wireOp",EDGE,"E42.17"),sQuery(id+"F17.wireOp",EDGE,"E42.18"),sQuery(id+"F17.wireOp",EDGE,"E42.19")])],"isStart":false});
            var sketch = newSketch(context, id + "F20", { "sketchPlane" : qUnion([Q0])});
            skCircle(sketch, "E43", {"center": v(-41.45, 12.82) * mm, "radius": 19.85 * mm});
            skCircle(sketch, "E44", {"center": v(-41.45, 12.82) * mm, "radius": 55 * mm, "construction": true});
            skCircle(sketch, "E45", {"center": v(-60.74, 64.32) * mm, "radius": 3.25 * mm});
            skCircle(sketch, "E46", {"center": v(-24.94, 65.28) * mm, "radius": 4.5 * mm});
            skCircle(sketch, "E47", {"center": v(11.5, 27.7) * mm, "radius": 4.5 * mm});
            skCircle(sketch, "E48", {"center": v(-1.96, 51.1) * mm, "radius": 4.5 * mm});
            skCircle(sketch, "E49", {"center": v(-63.45, -29.73) * mm, "radius": 6 * mm});
            skCircle(sketch, "E50", {"center": v(-31.45, -112.18) * mm, "radius": 15 * mm});
            skPoint(sketch, "E50.centerSnap0", {"position": v(-31.45, -144.18) * mm});
            skLineSegment(sketch, "E51.bottom", {"start": v(-14.2, -63.68) * mm, "end": v(-48.7, -63.68) * mm});
            skLineSegment(sketch, "E51.top", {"start": v(-14.2, -86.68) * mm, "end": v(-48.7, -86.68) * mm});
            skLineSegment(sketch, "E51.left", {"start": v(-14.2, -63.68) * mm, "end": v(-14.2, -86.68) * mm});
            skLineSegment(sketch, "E51.right", {"start": v(-48.7, -63.68) * mm, "end": v(-48.7, -86.68) * mm});
            skPoint(sketch, "E51.middle", {"position": v(-31.45, -75.18) * mm});
            skLineSegment(sketch, "E52.bottom", {"start": v(-7.95, 22.82) * mm, "end": v(-14.95, 22.82) * mm});
            skLineSegment(sketch, "E52.top", {"start": v(-7.95, 2.82) * mm, "end": v(-14.95, 2.82) * mm});
            skLineSegment(sketch, "E52.left", {"start": v(-7.95, 22.82) * mm, "end": v(-7.95, 2.82) * mm});
            skLineSegment(sketch, "E52.right", {"start": v(-14.95, 22.82) * mm, "end": v(-14.95, 2.82) * mm});
            skPoint(sketch, "E52.middle", {"position": v(-11.45, 12.82) * mm});
            skCircle(sketch, "E53", {"center": v(-57.7, 29.07) * mm, "radius": 1.25 * mm});
            skCircle(sketch, "E54", {"center": v(-25.2, 29.07) * mm, "radius": 1.25 * mm});
            skCircle(sketch, "E55", {"center": v(-25.2, -3.43) * mm, "radius": 1.25 * mm});
            skCircle(sketch, "E56", {"center": v(-57.7, -3.43) * mm, "radius": 1.25 * mm});
            skSolve(sketch);
        }
        {
            var Q0;
            Q0=makeQuery(id+"F20.imprint","IMPRINT",FACE,{"disambiguationData":[TD([[makeQuery(id+"F20.imprint","IMPRINT",EDGE,{"derivedFrom":sQuery(id+"F20.wireOp",EDGE,"E43")}),1.0]])]});
            var Q1;
            Q1=makeQuery(id+"F20.imprint","IMPRINT",FACE,{"disambiguationData":[TD([[makeQuery(id+"F20.imprint","IMPRINT",EDGE,{"derivedFrom":sQuery(id+"F20.wireOp",EDGE,"E52.bottom")}),1.0]])]});
            var Q2;
            Q2=makeQuery(id+"F20.imprint","IMPRINT",FACE,{"disambiguationData":[TD([[makeQuery(id+"F20.imprint","IMPRINT",EDGE,{"derivedFrom":sQuery(id+"F20.wireOp",EDGE,"E47")}),1.0]])]});
            var Q3;
            Q3=makeQuery(id+"F20.imprint","IMPRINT",FACE,{"disambiguationData":[TD([[makeQuery(id+"F20.imprint","IMPRINT",EDGE,{"derivedFrom":sQuery(id+"F20.wireOp",EDGE,"E48")}),1.0]])]});
            var Q4;
            Q4=makeQuery(id+"F20.imprint","IMPRINT",FACE,{"disambiguationData":[TD([[makeQuery(id+"F20.imprint","IMPRINT",EDGE,{"derivedFrom":sQuery(id+"F20.wireOp",EDGE,"E46")}),1.0]])]});
            var Q5;
            Q5=makeQuery(id+"F20.imprint","IMPRINT",FACE,{"disambiguationData":[TD([[makeQuery(id+"F20.imprint","IMPRINT",EDGE,{"derivedFrom":sQuery(id+"F20.wireOp",EDGE,"E45")}),1.0]])]});
            var Q6;
            Q6=makeQuery(id+"F20.imprint","IMPRINT",FACE,{"disambiguationData":[TD([[makeQuery(id+"F20.imprint","IMPRINT",EDGE,{"derivedFrom":sQuery(id+"F20.wireOp",EDGE,"E49")}),1.0]])]});
            var Q7;
            Q7=makeQuery(id+"F20.imprint","IMPRINT",FACE,{"disambiguationData":[TD([[makeQuery(id+"F20.imprint","IMPRINT",EDGE,{"derivedFrom":sQuery(id+"F20.wireOp",EDGE,"E51.bottom")}),1.0]])]});
            var Q8;
            Q8=makeQuery(id+"F20.imprint","IMPRINT",FACE,{"disambiguationData":[TD([[makeQuery(id+"F20.imprint","IMPRINT",EDGE,{"derivedFrom":sQuery(id+"F20.wireOp",EDGE,"E50")}),1.0]])]});
            var Q9;
            Q9=makeQuery(id+"F20.imprint","IMPRINT",FACE,{"disambiguationData":[TD([[makeQuery(id+"F20.imprint","IMPRINT",EDGE,{"derivedFrom":sQuery(id+"F20.wireOp",EDGE,"E53")}),1.0]])]});
            var Q10;
            Q10=makeQuery(id+"F20.imprint","IMPRINT",FACE,{"disambiguationData":[TD([[makeQuery(id+"F20.imprint","IMPRINT",EDGE,{"derivedFrom":sQuery(id+"F20.wireOp",EDGE,"E54")}),1.0]])]});
            var Q11;
            Q11=makeQuery(id+"F20.imprint","IMPRINT",FACE,{"disambiguationData":[TD([[makeQuery(id+"F20.imprint","IMPRINT",EDGE,{"derivedFrom":sQuery(id+"F20.wireOp",EDGE,"E56")}),1.0]])]});
            var Q12;
            Q12=makeQuery(id+"F20.imprint","IMPRINT",FACE,{"disambiguationData":[TD([[makeQuery(id+"F20.imprint","IMPRINT",EDGE,{"derivedFrom":sQuery(id+"F20.wireOp",EDGE,"E55")}),1.0]])]});
            extrude(context, id + "F21", {"entities" : qUnion([Q0, Q1, Q2, Q3, Q4, Q5, Q6, Q7, Q8, Q9, Q10, Q11, Q12]), "operationType" : NewBodyOperationType.REMOVE, "oppositeDirection" : true, "depth" : 25 * mm, "offsetDistance" : 25 * mm});
        }
    });
